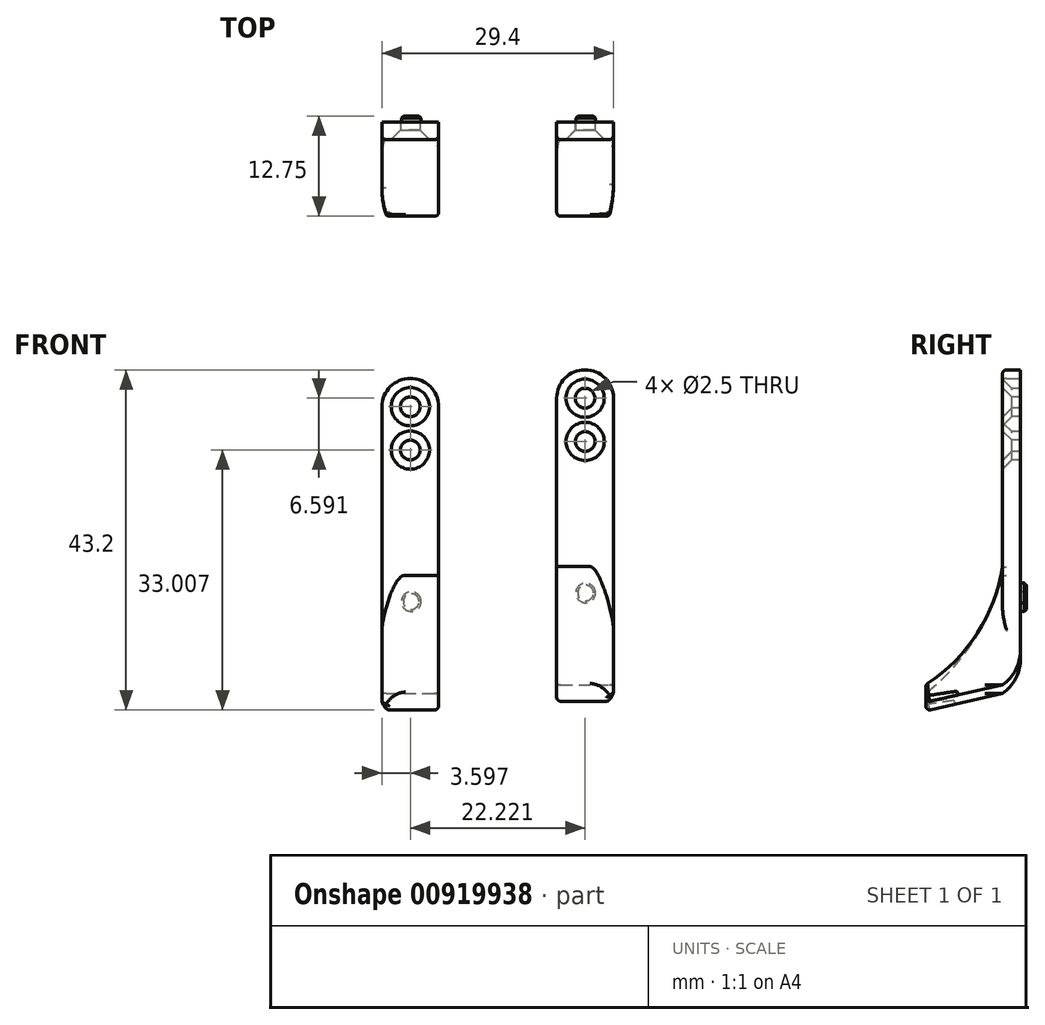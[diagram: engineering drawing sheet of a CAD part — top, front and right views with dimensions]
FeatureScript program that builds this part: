
annotation { "Feature Type Name" : "Feature", "Feature Type Description" : "" }
export const myFeature = defineFeature(function(context is Context, id is Id, definition is map)
    precondition{}
    {
        {
            var Q0;
            Q0=qCreatedBy(makeId("Front.planeOp"),FACE);
            var sketch = newSketch(context, id + "F0", { "sketchPlane" : qUnion([Q0])});
            skLineSegment(sketch, "E0.bottom", {"start": v(-46.46, 39.32) * mm, "end": v(-39.26, 39.32) * mm});
            skLineSegment(sketch, "E0.top", {"start": v(-46.46, 2.92) * mm, "end": v(-39.26, 2.92) * mm});
            skLineSegment(sketch, "E0.left", {"start": v(-46.46, 39.32) * mm, "end": v(-46.46, 2.92) * mm});
            skLineSegment(sketch, "E0.right", {"start": v(-39.26, 39.32) * mm, "end": v(-39.26, 2.92) * mm});
            skLineSegment(sketch, "E1.bottom", {"start": v(-24.26, 40.4) * mm, "end": v(-17.06, 40.4) * mm});
            skLineSegment(sketch, "E1.top", {"start": v(-24.26, 4) * mm, "end": v(-17.06, 4) * mm});
            skLineSegment(sketch, "E1.left", {"start": v(-24.26, 40.4) * mm, "end": v(-24.26, 4) * mm});
            skLineSegment(sketch, "E1.right", {"start": v(-17.06, 40.4) * mm, "end": v(-17.06, 4) * mm});
            skCircle(sketch, "E2", {"center": v(-42.86, 39.32) * mm, "radius": 3.6 * mm});
            skCircle(sketch, "E3", {"center": v(-20.66, 40.4) * mm, "radius": 3.6 * mm});
            skSolve(sketch);
        }
        {
            var Q0;
            Q0 = qSketchRegion(id + "F0", true);
            extrude(context, id + "F1", {"entities" : qUnion([Q0]), "depth" : 2.25 * mm, "offsetDistance" : 25 * mm});
        }
        {
            var Q0;
            Q0=makeQuery(id+"F1.opExtrude","SWEPT_FACE",FACE,{"disambiguationData":[OSD([sQuery(id+"F0.wireOp",EDGE,"E1.right")])]});
            var sketch = newSketch(context, id + "F2", { "sketchPlane" : qUnion([Q0])});
            skLineSegment(sketch, "E4", {"start": v(-2.25, 4) * mm, "end": v(-12, 1.77) * mm});
            skLineSegment(sketch, "E5", {"start": v(-12, 1.77) * mm, "end": v(-12, 4) * mm});
            skArc(sketch, "E6", {"start": v(-12, 4) * mm, "mid": v(-5.52, 10.46) * mm, "end": v(-2.25, 19) * mm});
            skSolve(sketch);
        }
        {
            var Q0;
            {var subQ0=sQuery(id+"F2.wireOp",EDGE,"E4");Q0=makeQuery(id+"F2.imprint","IMPRINT",FACE,{"disambiguationData":[TD([[makeQuery(id+"F2.imprint","IMPRINT",EDGE,{"derivedFrom":subQ0}),-1.0]])]});}
            extrude(context, id + "F3", {"entities" : qUnion([Q0]), "operationType" : NewBodyOperationType.ADD, "oppositeDirection" : true, "depth" : 7.2 * mm, "offsetDistance" : 25 * mm});
        }
        {
            var Q0;
            Q0=makeQuery(id+"F1.opExtrude","SWEPT_FACE",FACE,{"disambiguationData":[OSD([sQuery(id+"F0.wireOp",EDGE,"E0.left")])]});
            var sketch = newSketch(context, id + "F4", { "sketchPlane" : qUnion([Q0])});
            skLineSegment(sketch, "E7", {"start": v(2.25, 2.92) * mm, "end": v(12, 0.68) * mm});
            skLineSegment(sketch, "E8", {"start": v(12, 0.68) * mm, "end": v(12, 2.92) * mm});
            skArc(sketch, "E9", {"start": v(2.25, 17.92) * mm, "mid": v(5.89, 9.61) * mm, "end": v(12, 2.92) * mm});
            skSolve(sketch);
        }
        {
            var Q0;
            {var subQ0=sQuery(id+"F4.wireOp",EDGE,"E7");Q0=makeQuery(id+"F4.imprint","IMPRINT",FACE,{"disambiguationData":[TD([[makeQuery(id+"F4.imprint","IMPRINT",EDGE,{"derivedFrom":subQ0}),1.0]])]});}
            extrude(context, id + "F5", {"entities" : qUnion([Q0]), "operationType" : NewBodyOperationType.ADD, "oppositeDirection" : true, "depth" : 7.2 * mm, "offsetDistance" : 25 * mm});
        }
        {
            var Q0;
            Q0=makeQuery(id+"F1.opExtrude","CAP_FACE",FACE,{"disambiguationData":[OSD([sQuery(id+"F0.wireOp",EDGE,"E0.top"),sQuery(id+"F0.wireOp",EDGE,"E0.left"),sQuery(id+"F0.wireOp",EDGE,"E0.right"),sQuery(id+"F0.wireOp",EDGE,"E2")])],"isStart":false});
            var sketch = newSketch(context, id + "F6", { "sketchPlane" : qUnion([Q0])});
            skPoint(sketch, "E10", {"position": v(-42.86, 39.32) * mm});
            skPoint(sketch, "E11", {"position": v(-42.86, 33.82) * mm});
            skSolve(sketch);
        }
        {
            var Q0;
            Q0=makeQuery(id+"F1.opExtrude","CAP_FACE",FACE,{"disambiguationData":[OSD([sQuery(id+"F0.wireOp",EDGE,"E1.top"),sQuery(id+"F0.wireOp",EDGE,"E1.left"),sQuery(id+"F0.wireOp",EDGE,"E1.right"),sQuery(id+"F0.wireOp",EDGE,"E3")])],"isStart":false});
            var sketch = newSketch(context, id + "F7", { "sketchPlane" : qUnion([Q0])});
            skPoint(sketch, "E12", {"position": v(-20.66, 40.4) * mm});
            skPoint(sketch, "E13", {"position": v(-20.64, 34.9) * mm});
            skSolve(sketch);
        }
        {
            var Q0;
            Q0=sQuery(id+"F6.wireOp",VERTEX,"E10");
            var Q1;
            Q1=sQuery(id+"F6.wireOp",VERTEX,"E11");
            var Q2;
            Q2=makeQuery(id+"F1.opExtrude","SWEPT_BODY",BODY,{"disambiguationData":[OSD([sQuery(id+"F0.wireOp",EDGE,"E0.top"),sQuery(id+"F0.wireOp",EDGE,"E0.left"),sQuery(id+"F0.wireOp",EDGE,"E0.right"),sQuery(id+"F0.wireOp",EDGE,"E2")])]});
            hole(context, id + "F8", {"style" : HoleStyle.C_SINK, "endStyle" : HoleEndStyle.THROUGH, "holeDiameter" : 2.5 * mm, "cSinkDiameter" : 4.85 * mm, "cSinkAngle" : 90 * degree, "majorDiameter" : 5 * mm, "isTappedThrough" : true, "tappedDepth" : 12 * mm, "tapClearance" : 3, "locations" : qUnion([Q0, Q1]), "scope" : qUnion([Q2])});
        }
        {
            var Q0;
            Q0=sQuery(id+"F7.wireOp",VERTEX,"E12");
            var Q1;
            Q1=sQuery(id+"F7.wireOp",VERTEX,"E13");
            var Q2;
            Q2=makeQuery(id+"F1.opExtrude","SWEPT_BODY",BODY,{"disambiguationData":[OSD([sQuery(id+"F0.wireOp",EDGE,"E1.top"),sQuery(id+"F0.wireOp",EDGE,"E1.left"),sQuery(id+"F0.wireOp",EDGE,"E1.right"),sQuery(id+"F0.wireOp",EDGE,"E3")])]});
            hole(context, id + "F9", {"style" : HoleStyle.C_SINK, "endStyle" : HoleEndStyle.THROUGH, "holeDiameter" : 2.5 * mm, "cSinkDiameter" : 4.85 * mm, "cSinkAngle" : 90 * degree, "majorDiameter" : 5 * mm, "isTappedThrough" : true, "tappedDepth" : 12 * mm, "tapClearance" : 3, "locations" : qUnion([Q0, Q1]), "scope" : qUnion([Q2])});
        }
        {
            var Q0;
            Q0=makeQuery(id+"F1.opExtrude","CAP_FACE",FACE,{"disambiguationData":[OSD([sQuery(id+"F0.wireOp",EDGE,"E1.top"),sQuery(id+"F0.wireOp",EDGE,"E1.left"),sQuery(id+"F0.wireOp",EDGE,"E1.right"),sQuery(id+"F0.wireOp",EDGE,"E3")])],"isStart":true});
            var sketch = newSketch(context, id + "F10", { "sketchPlane" : qUnion([Q0])});
            skCircle(sketch, "E14", {"center": v(20.59, 15.66) * mm, "radius": 1.25 * mm});
            skSolve(sketch);
        }
        {
            var Q0;
            Q0 = qSketchRegion(id + "F10", true);
            extrude(context, id + "F11", {"entities" : qUnion([Q0]), "operationType" : NewBodyOperationType.ADD, "depth" : .75 * mm, "offsetDistance" : 25 * mm});
        }
        {
            var Q0;
            Q0=makeQuery(id+"F1.opExtrude","CAP_FACE",FACE,{"disambiguationData":[OSD([sQuery(id+"F0.wireOp",EDGE,"E0.top"),sQuery(id+"F0.wireOp",EDGE,"E0.left"),sQuery(id+"F0.wireOp",EDGE,"E0.right"),sQuery(id+"F0.wireOp",EDGE,"E2")])],"isStart":true});
            var sketch = newSketch(context, id + "F12", { "sketchPlane" : qUnion([Q0])});
            skCircle(sketch, "E15", {"center": v(42.75, 14.57) * mm, "radius": 1.25 * mm});
            skSolve(sketch);
        }
        {
            var Q0;
            Q0 = qSketchRegion(id + "F12", true);
            extrude(context, id + "F13", {"entities" : qUnion([Q0]), "operationType" : NewBodyOperationType.ADD, "depth" : .75 * mm, "offsetDistance" : 25 * mm});
        }
        {
            var Q0;
            Q0=makeQuery(id+"F13.opExtrude","CAP_EDGE",EDGE,{"disambiguationData":[OSD([sQuery(id+"F12.wireOp",EDGE,"E15")])],"isStart":false});
            chamfer(context, id + "F14", {"entities" : qUnion([Q0]), "width" : .25 * mm, "tangentPropagation" : true});
        }
        {
            var Q0;
            Q0=makeQuery(id+"F11.opExtrude","CAP_EDGE",EDGE,{"disambiguationData":[OSD([sQuery(id+"F10.wireOp",EDGE,"E14")])],"isStart":false});
            chamfer(context, id + "F15", {"entities" : qUnion([Q0]), "width" : .25 * mm, "tangentPropagation" : true});
        }
        {
            var Q0;
            Q0=makeQuery(id+"F5.opExtrude","CAP_EDGE",EDGE,{"disambiguationData":[OSD([sQuery(id+"F4.wireOp",EDGE,"E9")])],"isStart":true});
            fillet(context, id + "F16", {"entities" : qUnion([Q0]), "radius" : 3 * mm, "tangentPropagation" : true, "allowEdgeOverflow" : false});
        }
        {
            var Q0;
            Q0=makeQuery(id+"F3.opExtrude","CAP_EDGE",EDGE,{"disambiguationData":[OSD([sQuery(id+"F2.wireOp",EDGE,"E6")])],"isStart":true});
            fillet(context, id + "F17", {"entities" : qUnion([Q0]), "radius" : 3 * mm, "tangentPropagation" : true, "allowEdgeOverflow" : false});
        }
        {
            var Q0;
            Q0=makeQuery(id+"F3.opExtrude","SWEPT_EDGE",EDGE,{"disambiguationData":[OSD([sQuery(id+"F2.wireOp",EDGE,"E4"),sQuery(id+"F2.wireOp",EDGE,"E5")])]});
            var Q1;
            Q1=makeQuery(id+"F3.opExtrude","CAP_EDGE",EDGE,{"disambiguationData":[OSD([sQuery(id+"F2.wireOp",EDGE,"E5")])],"isStart":false});
            var Q2;
            Q2=makeQuery(id+"F5.opExtrude","SWEPT_EDGE",EDGE,{"disambiguationData":[OSD([sQuery(id+"F4.wireOp",EDGE,"E7"),sQuery(id+"F4.wireOp",EDGE,"E8")])]});
            var Q3;
            Q3=makeQuery(id+"F5.opExtrude","CAP_EDGE",EDGE,{"disambiguationData":[OSD([sQuery(id+"F4.wireOp",EDGE,"E8")])],"isStart":false});
            var Q4;
            Q4=makeQuery(id+"F3.opExtrude","SWEPT_EDGE",EDGE,{"disambiguationData":[OSD([sQuery(id+"F2.wireOp",EDGE,"E5"),sQuery(id+"F2.wireOp",EDGE,"E6")])]});
            var Q5;
            Q5=makeQuery(id+"F5.opExtrude","SWEPT_EDGE",EDGE,{"disambiguationData":[OSD([sQuery(id+"F4.wireOp",EDGE,"E8"),sQuery(id+"F4.wireOp",EDGE,"E9")])]});
            var Q6;
            Q6=makeQuery(id+"F5.opExtrude","CAP_EDGE",EDGE,{"disambiguationData":[OSD([sQuery(id+"F4.wireOp",EDGE,"E9")])],"isStart":false});
            var Q7;
            Q7=makeQuery(id+"F3.opExtrude","CAP_EDGE",EDGE,{"disambiguationData":[OSD([sQuery(id+"F2.wireOp",EDGE,"E6")])],"isStart":false});
            var Q8;
            Q8=makeQuery(id+"F1.opExtrude","CAP_EDGE",EDGE,{"disambiguationData":[OSD([sQuery(id+"F0.wireOp",EDGE,"E0.left")])],"isStart":false});
            var Q9;
            Q9=makeQuery(id+"F1.opExtrude","CAP_EDGE",EDGE,{"disambiguationData":[OSD([sQuery(id+"F0.wireOp",EDGE,"E1.left")])],"isStart":false});
            var Q10;
            Q10=makeQuery(id+"F3.opExtrude","CAP_EDGE",EDGE,{"disambiguationData":[OSD([sQuery(id+"F2.wireOp",EDGE,"E4")])],"isStart":false});
            var Q11;
            Q11=makeQuery(id+"F5.opExtrude","CAP_EDGE",EDGE,{"disambiguationData":[OSD([sQuery(id+"F4.wireOp",EDGE,"E7")])],"isStart":false});
            var Q12;
            Q12=makeQuery(id+"F3.opExtrude","CAP_EDGE",EDGE,{"disambiguationData":[OSD([sQuery(id+"F2.wireOp",EDGE,"E4")])],"isStart":true});
            var Q13;
            Q13=makeQuery(id+"F5.opExtrude","CAP_EDGE",EDGE,{"disambiguationData":[OSD([sQuery(id+"F4.wireOp",EDGE,"E7")])],"isStart":true});
            fillet(context, id + "F18", {"entities" : qUnion([Q0, Q1, Q2, Q3, Q4, Q5, Q6, Q7, Q8, Q9, Q10, Q11, Q12, Q13]), "radius" : .5 * mm, "tangentPropagation" : true, "allowEdgeOverflow" : false});
        }
        {
            var Q0;
            Q0=makeQuery(id+"F1.opExtrude","CAP_EDGE",EDGE,{"disambiguationData":[OSD([sQuery(id+"F0.wireOp",EDGE,"E0.top")])],"isStart":true});
            var Q1;
            Q1=makeQuery(id+"F1.opExtrude","CAP_EDGE",EDGE,{"disambiguationData":[OSD([sQuery(id+"F0.wireOp",EDGE,"E1.top")])],"isStart":true});
            fillet(context, id + "F19", {"entities" : qUnion([Q0, Q1]), "radius" : 5 * mm, "tangentPropagation" : true, "allowEdgeOverflow" : false});
        }
    });
